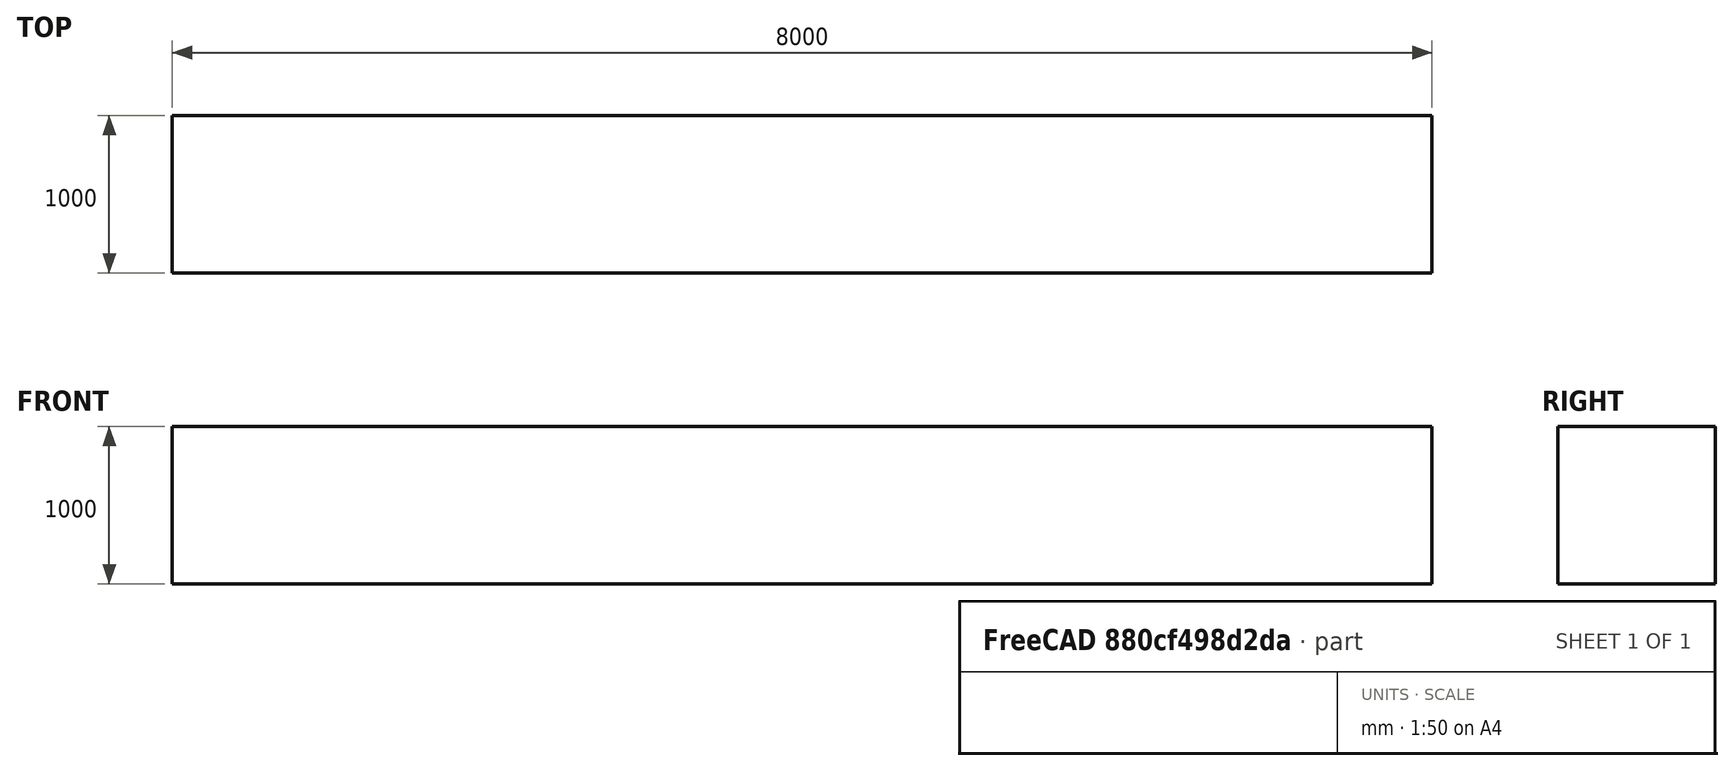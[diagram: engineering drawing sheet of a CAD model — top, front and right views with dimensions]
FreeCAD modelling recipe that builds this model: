
FCSTD DOCUMENT  (FreeCAD 0.17R13142 (Git))
Label: FemCalculixCantilever3D
License: CC-BY 3.0
LicenseURL: http://creativecommons.org/licenses/by/3.0/
objects: Part::Box×1, Fem::FemMeshShapeNetgenObject×1, Fem::ConstraintFixed×1, Fem::ConstraintForce×1, Fem::FemSolverObjectPython×1, App::MaterialObjectPython×1, Fem::FemMeshObjectPython×1, Fem::FemResultObjectPython×1, Fem::FemAnalysis×1
note: 1 computed .brp shape members not serialized (recipe doc carries the construction recipe); baked Part::Feature solids carry a one-line shape summary decoded from their .brp

FEATURE [Part::Box] Box  label="Cube"
  AttacherType = Attacher::AttachEngine3D
  Height = 1000
  Length = 8000
  Width = 1000
FEATURE [Fem::FemMeshShapeNetgenObject] Box_Mesh
  Fineness = 2
  GrowthRate = 0.3
  MaxSize = 750
  NbSegsPerEdge = 1
  NbSegsPerRadius = 2
  Optimize = true
  SecondOrder = true
  Shape = -> Box
FEATURE [Fem::ConstraintFixed] FemConstraintFixed
  NormalDirection = (-1,0,0)
  Normals = (16) [(-1,0,0),(-1,0,0),(-1,0,0),(-1,0,0),(-1,0,0),(-1,0,0),(-1,0,0),(-1,0,0),(-1,0,0),(-1,0,0),(-1,0,0),(-1,0,0),(-1,0,0),(-1,0,0),(-1,0,0),(-1,0,0)]
  Points = (16) [(0,1000,0),(0,1000,333.333),(0,1000,666.667),(0,1000,1000),(0,666.667,0),(0,666.667,333.333),(0,666.667,666.667),(0,666.667,1000),(0,333.333,0),+7 more]
  References = -> [Box]
  Scale = 33
FEATURE [Fem::ConstraintForce] FemConstraintForce
  Direction = -> Box [Edge7]
  DirectionVector = (0,0,-1)
  Force = 9000000
  NormalDirection = (1,0,0)
  Points = (16) [(8000,1000,0),(8000,1000,333.333),(8000,1000,666.667),(8000,1000,1000),(8000,666.667,0),(8000,666.667,333.333),(8000,666.667,666.667),+9 more]
  References = -> [Box]
  Reversed = true
  Scale = 33
FEATURE [Fem::FemSolverObjectPython] CalculiXccxTools  # FEM object (typed FeaturePython)
  AnalysisType = 0
  BeamShellResultOutput3D = false
  EigenmodeHighLimit = 0
  EigenmodeLowLimit = 0
  EigenmodesCount = 15
  GeometricalNonlinearity = 0
  IterationsControlParameterCutb = 0.25,0.5,0.75,0.85,,,1.5,
  IterationsControlParameterIter = 4,8,9,200,10,400,,200,,
  IterationsControlParameterTimeUse = false
  IterationsThermoMechMaximum = 2000
  IterationsUserDefinedIncrementations = false
  IterationsUserDefinedTimeStepLength = false
  MaterialNonlinearity = 0
  MatrixSolverType = 0
  SplitInputWriter = false
  ThermoMechSteadyState = true
  TimeEnd = 1
  TimeInitialStep = 1
FEATURE [App::MaterialObjectPython] SolidMaterial  # material (typed FeaturePython)
  Category = 0
  Material = Density=7900.0 kg/m^3,Description=Standard steel material for CalculiX sample calculations,Father=Metal,Name=CalculiX-Steel,PoissonRatio=0.3,+4 more (map truncated)
FEATURE [Fem::FemMeshObjectPython] Result_mesh  # FEM object (typed FeaturePython)
FEATURE [Fem::FemResultObjectPython] CalculiX_static_results  # FEM object (typed FeaturePython)
  DisplacementLengths = [87.293,87.2919,87.2871,87.303,0,0,0,0,1.69117,4.749,9.48987,15.7836,23.4448,32.2894,42.1378,52.765,63.9816,75.6043,1.71227,4.76323,9.49458,15.7841,23.4563,32.3006,42.1436,52.7686,63.9856,75.605,1.69987,4.76597,9.50272,15.789,23.4497,32.3,+194 more]
  DisplacementVectors = (228) [(-8.12414,0.0331274,-86.9141),(8.10954,0.0194004,-86.9144),(-8.11693,0.0156184,-86.9089),(8.129,0.0338889,-86.9237),(0,0,0),(0,0,0),(0,0,0),(0,0,0),+220 more]
  Eigenmode = 0
  EigenmodeFrequency = 0
  MaxShear = [7.33595,10.9318,8.01827,10.8807,152.921,163.005,169.475,158.112,197.819,181.444,164.244,141.348,120.647,103.056,80.1779,60.5748,44.2206,24.3806,208.52,175.852,156.526,141.882,121.387,99.8073,81.9904,59.2077,38.7336,24.0413,208.845,181.85,+198 more]
  Mesh = -> Result_mesh
  NodeNumbers = [1,2,3,4,5,6,7,8,9,10,11,12,13,14,15,16,17,18,19,20,21,22,23,24,25,26,27,28,29,30,31,32,33,34,35,36,37,38,39,40,41,42,43,44,45,46,47,48,49,50,51,52,53,54,55,56,57,58,59,60,61,62,63,64,65,66,67,68,69,+159 more]
  PrincipalMax = [9.97903,8.99203,8.89773,12.9951,-160.829,456.549,-120.75,459.98,385.212,350.411,317.806,275.207,229.294,193.188,151.933,110.596,76.0149,40.8184,393.488,346.829,307.17,274.943,236.213,192.972,157.654,112.139,71.556,39.9121,16.2892,4.65084,+198 more]
  PrincipalMed = [-4.53591,8.21859,-3.71528,4.13137,-213.489,166.309,-178.808,186.152,11.8116,12.4961,10.2584,6.82189,12.3946,10.3428,10.8132,10.4906,11.3385,7.74391,-8.5951,7.72476,8.06166,8.69887,4.64854,5.67608,7.62016,6.64117,7.90148,7.79936,-5.06381,+199 more]
  PrincipalMin = [-4.69287,-12.8716,-7.13881,-8.76626,-466.672,130.54,-459.699,143.755,-10.4265,-12.4774,-10.6829,-7.48891,-12.0001,-12.9242,-8.42286,-10.5532,-12.4263,-7.94273,-23.551,-4.87505,-5.88217,-8.82024,-6.55961,-6.64258,-6.32677,-6.27605,-5.91115,+201 more]
  ResultType = Fem::FemResultMechanical
  Stats = [-8.13222,-0.0202412,8.12992,-0.287103,0.0104694,0.295963,-86.9271,-33.5258,0,0,33.8878,87.3065,11.6387,142.701,409.766,-160.829,74.2152,463.872,-242.571,-0.0301983,241.01,-466.672,-74.6947,155.622,6.61053,74.455,208.845,0,0,0,0,0,0,0,0,0,0,+2 more]
  StrainVectors = (228) [(-2.94247e-05,1.11828e-05,1.9671e-05),(4.37605e-05,-1.47758e-05,-2.07199e-05),(-4.06178e-05,2.38269e-05,1.30645e-05),+225 more]
  StressValues = [14.5941,21.4874,14.6284,18.9535,283.208,309.678,313.973,297.302,385.001,351.068,318.535,275.819,230.069,195.519,151.656,112.119,79.2769,43.114,409.766,345.577,306.319,275.422,237.368,193.749,157.471,112.514,71.5676,42.4158,407.433,357.24,+198 more]
  StressVectors = (228) [(-4.58009,1.97958,3.35076),(8.0703,-1.38556,-2.34576),(-7.0128,3.39749,1.65895),(12.8688,-2.00846,-2.50015),(-452.84,-194.075,-194.075),+223 more]
  Time = 0
FEATURE [Fem::FemAnalysis] Analysis
  Group = -> [CalculiXccxTools,SolidMaterial,FemConstraintFixed,FemConstraintForce,Box_Mesh,CalculiX_static_results]
